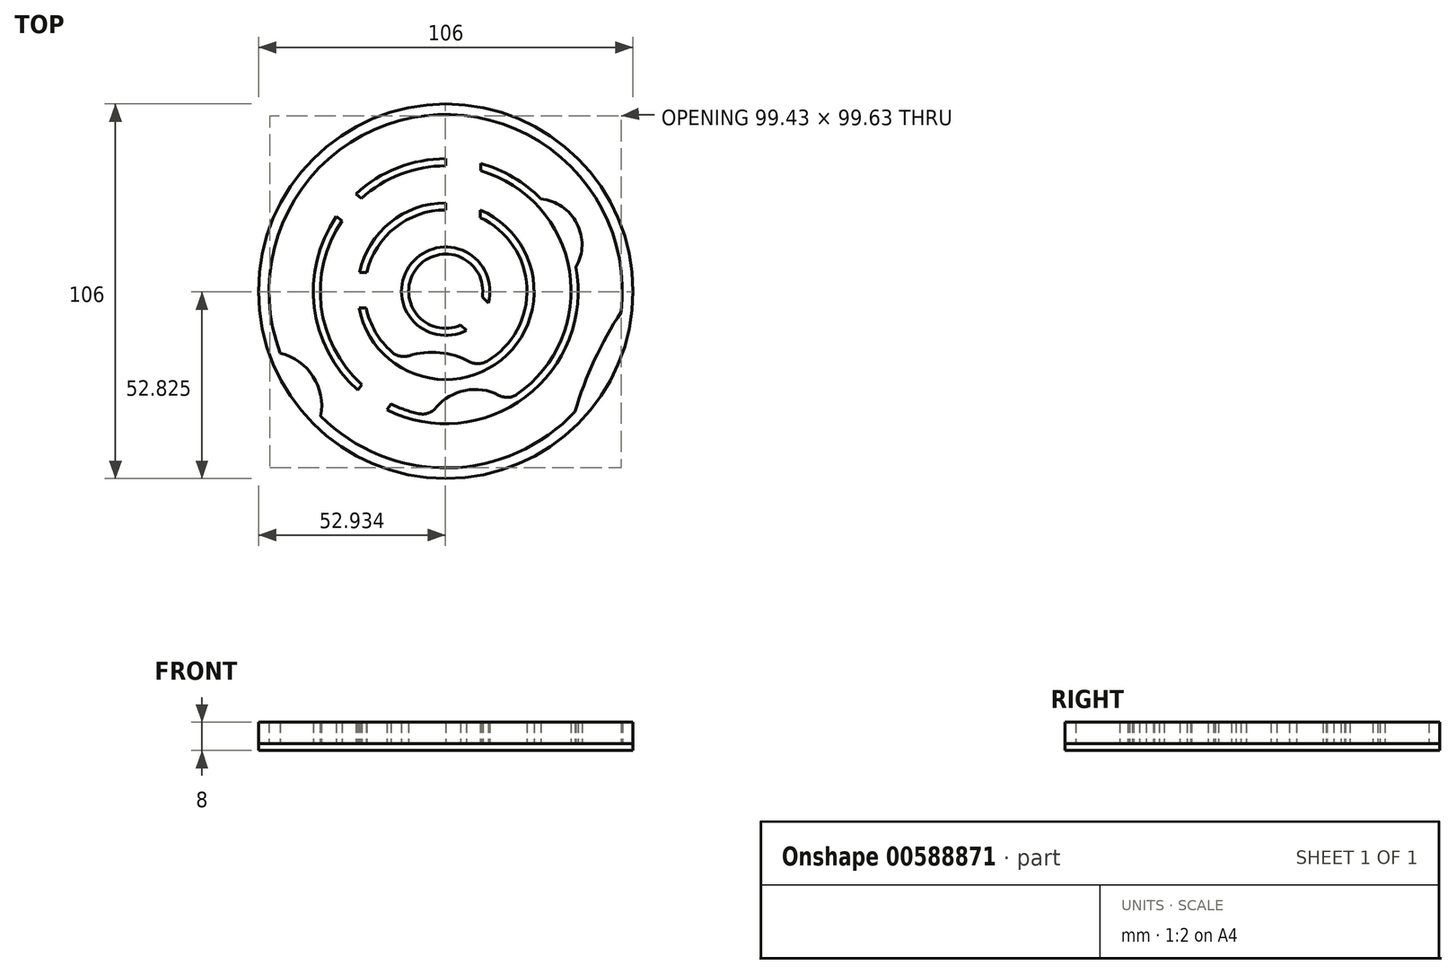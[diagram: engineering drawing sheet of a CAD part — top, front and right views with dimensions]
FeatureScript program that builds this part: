
annotation { "Feature Type Name" : "Feature", "Feature Type Description" : "" }
export const myFeature = defineFeature(function(context is Context, id is Id, definition is map)
    precondition{}
    {
        {
            var Q0;
            Q0=qCreatedBy(makeId("Top.planeOp"),FACE);
            var sketch = newSketch(context, id + "F0", { "sketchPlane" : qUnion([Q0])});
            skArc(sketch, "E0", {"start": v(49.65, -5.93) * mm, "mid": v(-5.98, 49.64) * mm, "end": v(-46.82, -17.54) * mm});
            skArc(sketch, "E1", {"start": v(0, 37.5) * mm, "mid": v(-13.64, 34.93) * mm, "end": v(-25.42, 27.57) * mm});
            skArc(sketch, "E2.0", {"start": v(0, 35.5) * mm, "mid": v(-12.79, 33.12) * mm, "end": v(-23.85, 26.3) * mm});
            skArc(sketch, "E3.0", {"start": v(-24.55, -4.72) * mm, "mid": v(15.72, -19.44) * mm, "end": v(9.76, 23.02) * mm});
            skArc(sketch, "E4.0", {"start": v(-22.51, -4.72) * mm, "mid": v(-19.88, -11.56) * mm, "end": v(-15.24, -17.23) * mm});
            skArc(sketch, "E5", {"start": v(12.06, -3.28) * mm, "mid": v(-9.74, 7.83) * mm, "end": v(5.8, -11.07) * mm});
            skArc(sketch, "E6.0", {"start": v(10.36, -1.72) * mm, "mid": v(-8.29, 6.45) * mm, "end": v(4.22, -9.62) * mm});
            skLineSegment(sketch, "E7", {"start": v(9.9, 36.17) * mm, "end": v(9.9, 34.1) * mm});
            skLineSegment(sketch, "E8", {"start": v(0, 37.5) * mm, "end": v(0, 35.5) * mm});
            skLineSegment(sketch, "E9", {"start": v(-24.44, 5.28) * mm, "end": v(-22.39, 5.28) * mm});
            skLineSegment(sketch, "E10", {"start": v(-24.55, -4.72) * mm, "end": v(-22.51, -4.72) * mm});
            skLineSegment(sketch, "E11", {"start": v(4.22, -9.62) * mm, "end": v(5.8, -11.07) * mm});
            skLineSegment(sketch, "E12", {"start": v(10.36, -1.72) * mm, "end": v(12.06, -3.28) * mm});
            skLineSegment(sketch, "E13", {"start": v(-24.94, -28) * mm, "end": v(-23.75, -26.38) * mm});
            skLineSegment(sketch, "E14", {"start": v(-16.66, -33.6) * mm, "end": v(-15.45, -31.96) * mm});
            skArc(sketch, "E15.trimOffspring", {"start": v(-15.45, -31.96) * mm, "mid": v(-11.63, -33.54) * mm, "end": v(-7.66, -34.66) * mm});
            skArc(sketch, "E16.trimOffspring", {"start": v(-16.66, -33.6) * mm, "mid": v(22.6, -29.92) * mm, "end": v(36.87, 6.84) * mm});
            skLineSegment(sketch, "E17", {"start": v(0, 23) * mm, "end": v(0, 25) * mm});
            skLineSegment(sketch, "E18", {"start": v(9.76, 20.83) * mm, "end": v(9.76, 23.02) * mm});
            skArc(sketch, "E19.trimOffspring", {"start": v(0, 23) * mm, "mid": v(-14.28, 18.03) * mm, "end": v(-22.39, 5.28) * mm});
            skArc(sketch, "E20.trimOffspring", {"start": v(0, 25) * mm, "mid": v(-15.7, 19.45) * mm, "end": v(-24.44, 5.28) * mm});
            skLineSegment(sketch, "E21", {"start": v(-29.38, 19.93) * mm, "end": v(-30.97, 21.15) * mm});
            skLineSegment(sketch, "E22", {"start": v(-23.85, 26.3) * mm, "end": v(-25.42, 27.57) * mm});
            skArc(sketch, "E23.trimOffspring", {"start": v(-29.38, 19.93) * mm, "mid": v(-35.24, -4.28) * mm, "end": v(-23.75, -26.38) * mm});
            skArc(sketch, "E24.trimOffspring", {"start": v(-30.97, 21.15) * mm, "mid": v(-37.22, -4.56) * mm, "end": v(-24.94, -28) * mm});
            skCircle(sketch, "E25.0", {"center": v(0, 0) * mm, "radius": 53 * mm});
            skArc(sketch, "E26", {"start": v(49.65, -5.93) * mm, "mid": v(42.1, -19.5) * mm, "end": v(36.62, -34.05) * mm});
            skArc(sketch, "E27", {"start": v(36.87, 6.84) * mm, "mid": v(37.14, 19.18) * mm, "end": v(26.93, 26.1) * mm});
            skArc(sketch, "E28", {"start": v(-35.4, -35.32) * mm, "mid": v(-37.54, -24.14) * mm, "end": v(-46.82, -17.54) * mm});
            skArc(sketch, "E29", {"start": v(15.05, -29.47) * mm, "mid": v(5.54, -28.06) * mm, "end": v(-2.73, -32.98) * mm});
            skArc(sketch, "E30", {"start": v(6.76, -19.93) * mm, "mid": v(-1.68, -17.38) * mm, "end": v(-10.46, -18.26) * mm});
            skArc(sketch, "E31.trimOffspring", {"start": v(11.65, -19.83) * mm, "mid": v(22.98, 1.07) * mm, "end": v(9.76, 20.83) * mm});
            skArc(sketch, "E32.trimOffspring", {"start": v(20.25, -29.16) * mm, "mid": v(35.03, 5.73) * mm, "end": v(9.9, 34.1) * mm});
            skArc(sketch, "E33.filletArc", {"start": v(6.76, -19.93) * mm, "mid": v(9.22, -20.52) * mm, "end": v(11.65, -19.83) * mm});
            skArc(sketch, "E34.filletArc", {"start": v(-15.24, -17.23) * mm, "mid": v(-12.98, -18.37) * mm, "end": v(-10.46, -18.26) * mm});
            skArc(sketch, "E35.filletArc", {"start": v(-7.66, -34.66) * mm, "mid": v(-4.96, -34.51) * mm, "end": v(-2.73, -32.98) * mm});
            skArc(sketch, "E36.filletArc", {"start": v(15.05, -29.47) * mm, "mid": v(17, -30.03) * mm, "end": v(19.03, -29.78) * mm});
            skArc(sketch, "E37.filletArc", {"start": v(19.03, -29.78) * mm, "mid": v(19.66, -29.5) * mm, "end": v(20.25, -29.16) * mm});
            skArc(sketch, "E38.trimOffspring", {"start": v(26.93, 26.1) * mm, "mid": v(19.1, 32.28) * mm, "end": v(9.9, 36.17) * mm});
            skArc(sketch, "E39.trimOffspring", {"start": v(-35.4, -35.32) * mm, "mid": v(0.88, -50) * mm, "end": v(36.62, -34.05) * mm});
            skPoint(sketch, "E40.orphan", {"position": v(0, 31.05) * mm});
            skPoint(sketch, "E41.orphan", {"position": v(9.76, 31.05) * mm});
            skSolve(sketch);
        }
        {
            var Q0;
            Q0=makeQuery(id+"F0.imprint","IMPRINT",FACE,{"disambiguationData":[TD([[makeQuery(id+"F0.imprint","IMPRINT",EDGE,{"derivedFrom":sQuery(id+"F0.wireOp",EDGE,"E0")}),-1.0]])]});
            var Q1;
            Q1=makeQuery(id+"F0.imprint","IMPRINT",FACE,{"disambiguationData":[TD([[makeQuery(id+"F0.imprint","IMPRINT",EDGE,{"derivedFrom":sQuery(id+"F0.wireOp",EDGE,"E13")}),1.0]])]});
            var Q2;
            Q2=makeQuery(id+"F0.imprint","IMPRINT",FACE,{"disambiguationData":[TD([[makeQuery(id+"F0.imprint","IMPRINT",EDGE,{"derivedFrom":sQuery(id+"F0.wireOp",EDGE,"E1")}),1.0]])]});
            var Q3;
            Q3=makeQuery(id+"F0.imprint","IMPRINT",FACE,{"disambiguationData":[TD([[makeQuery(id+"F0.imprint","IMPRINT",EDGE,{"derivedFrom":sQuery(id+"F0.wireOp",EDGE,"E7")}),1.0]])]});
            var Q4;
            Q4=makeQuery(id+"F0.imprint","IMPRINT",FACE,{"disambiguationData":[TD([[makeQuery(id+"F0.imprint","IMPRINT",EDGE,{"derivedFrom":sQuery(id+"F0.wireOp",EDGE,"E3.0")}),1.0]])]});
            var Q5;
            Q5=makeQuery(id+"F0.imprint","IMPRINT",FACE,{"disambiguationData":[TD([[makeQuery(id+"F0.imprint","IMPRINT",EDGE,{"derivedFrom":sQuery(id+"F0.wireOp",EDGE,"E5")}),1.0]])]});
            var Q6;
            Q6=makeQuery(id+"F0.imprint","IMPRINT",FACE,{"disambiguationData":[TD([[makeQuery(id+"F0.imprint","IMPRINT",EDGE,{"derivedFrom":sQuery(id+"F0.wireOp",EDGE,"E9")}),1.0]])]});
            extrude(context, id + "F1", {"entities" : qUnion([Q0, Q1, Q2, Q3, Q4, Q5, Q6]), "depth" : 6 * mm, "offsetDistance" : 25 * mm});
        }
        {
            var Q0;
            Q0=qCreatedBy(makeId("Top.planeOp"),FACE);
            var sketch = newSketch(context, id + "F2", { "sketchPlane" : qUnion([Q0])});
            skCircle(sketch, "E42.0", {"center": v(0, 0) * mm, "radius": 53 * mm});
            skSolve(sketch);
        }
        {
            var Q0;
            Q0 = qSketchRegion(id + "F2", true);
            extrude(context, id + "F3", {"entities" : qUnion([Q0]), "oppositeDirection" : true, "depth" : 2 * mm, "offsetDistance" : 25 * mm});
        }
    });
